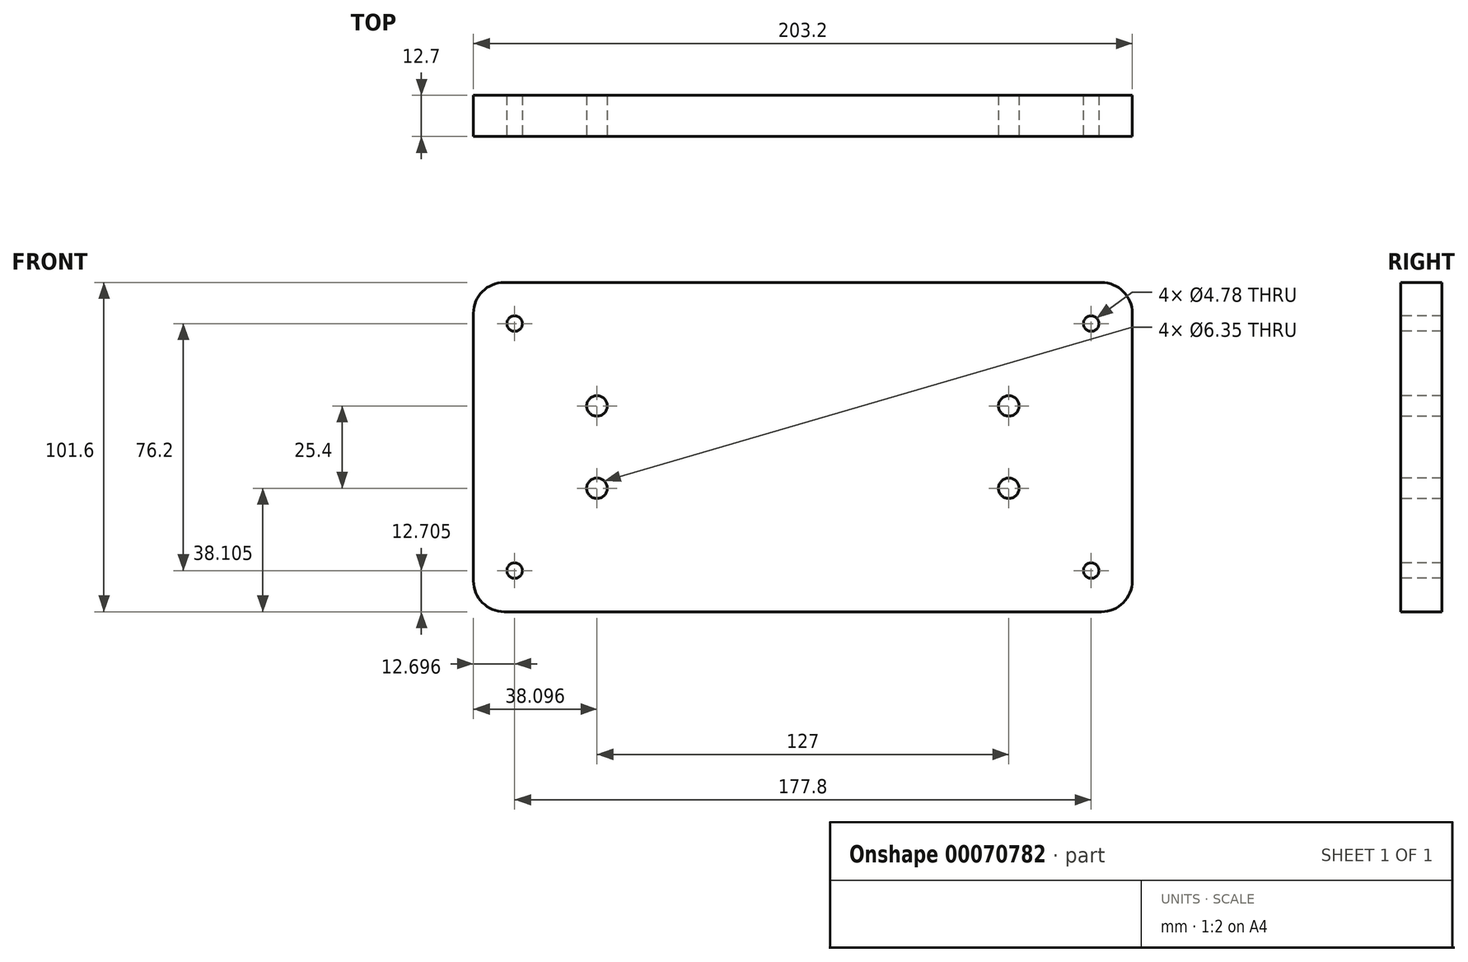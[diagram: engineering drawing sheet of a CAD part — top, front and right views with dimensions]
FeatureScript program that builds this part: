
annotation { "Feature Type Name" : "Feature", "Feature Type Description" : "" }
export const myFeature = defineFeature(function(context is Context, id is Id, definition is map)
    precondition{}
    {
        {
            var Q0;
            Q0=qCreatedBy(makeId("Front.planeOp"),FACE);
            var sketch = newSketch(context, id + "F0", { "sketchPlane" : qUnion([Q0])});
            skLineSegment(sketch, "E0.bottom", {"start": v(-101.78, -32.92) * mm, "end": v(101.42, -32.92) * mm});
            skLineSegment(sketch, "E0.top", {"start": v(-101.78, 68.68) * mm, "end": v(101.42, 68.68) * mm});
            skLineSegment(sketch, "E0.left", {"start": v(-101.78, -32.92) * mm, "end": v(-101.78, 68.68) * mm});
            skLineSegment(sketch, "E0.right", {"start": v(101.42, -32.92) * mm, "end": v(101.42, 68.68) * mm});
            skSolve(sketch);
        }
        {
            var Q0;
            Q0 = qSketchRegion(id + "F0", true);
            extrude(context, id + "F1", {"entities" : qUnion([Q0]), "depth" : 12.7 * mm});
        }
        {
            var Q0;
            Q0=makeQuery(id+"F1.opExtrude","SWEPT_EDGE",EDGE,{"disambiguationData":[OSD([sQuery(id+"F0.wireOp",EDGE,"E0.top"),sQuery(id+"F0.wireOp",EDGE,"E0.left")])]});
            var Q1;
            Q1=makeQuery(id+"F1.opExtrude","SWEPT_EDGE",EDGE,{"disambiguationData":[OSD([sQuery(id+"F0.wireOp",EDGE,"E0.top"),sQuery(id+"F0.wireOp",EDGE,"E0.right")])]});
            var Q2;
            Q2=makeQuery(id+"F1.opExtrude","SWEPT_EDGE",EDGE,{"disambiguationData":[OSD([sQuery(id+"F0.wireOp",EDGE,"E0.bottom"),sQuery(id+"F0.wireOp",EDGE,"E0.right")])]});
            var Q3;
            Q3=makeQuery(id+"F1.opExtrude","SWEPT_EDGE",EDGE,{"disambiguationData":[OSD([sQuery(id+"F0.wireOp",EDGE,"E0.bottom"),sQuery(id+"F0.wireOp",EDGE,"E0.left")])]});
            fillet(context, id + "F2", {"entities" : qUnion([Q0, Q1, Q2, Q3]), "radius" : 9.52 * mm, "tangentPropagation" : true, "allowEdgeOverflow" : false});
        }
        {
            var Q0;
            Q0=makeQuery(id+"F1.opExtrude","CAP_FACE",FACE,{"disambiguationData":[OSD([sQuery(id+"F0.wireOp",EDGE,"E0.bottom"),sQuery(id+"F0.wireOp",EDGE,"E0.top"),sQuery(id+"F0.wireOp",EDGE,"E0.left"),sQuery(id+"F0.wireOp",EDGE,"E0.right")])],"isStart":false});
            var sketch = newSketch(context, id + "F3", { "sketchPlane" : qUnion([Q0])});
            skPoint(sketch, "E1", {"position": v(-89.08, -20.22) * mm});
            skPoint(sketch, "E2", {"position": v(-89.08, 55.98) * mm});
            skPoint(sketch, "E3", {"position": v(88.72, 55.98) * mm});
            skPoint(sketch, "E4", {"position": v(88.72, -20.22) * mm});
            skSolve(sketch);
        }
        {
            var Q0;
            Q0=sQuery(id+"F3.wireOp",VERTEX,"E2");
            var Q1;
            Q1=sQuery(id+"F3.wireOp",VERTEX,"E1");
            var Q2;
            Q2=sQuery(id+"F3.wireOp",VERTEX,"E4");
            var Q3;
            Q3=sQuery(id+"F3.wireOp",VERTEX,"E3");
            var Q4;
            Q4=makeQuery(id+"F1.opExtrude","SWEPT_BODY",BODY,{"disambiguationData":[OSD([sQuery(id+"F0.wireOp",EDGE,"E0.bottom"),sQuery(id+"F0.wireOp",EDGE,"E0.top"),sQuery(id+"F0.wireOp",EDGE,"E0.left"),sQuery(id+"F0.wireOp",EDGE,"E0.right")])]});
            hole(context, id + "F4", {"style" : HoleStyle.SIMPLE, "holeDiameter" : 4.78 * mm, "endStyle" : HoleEndStyle.THROUGH, "locations" : qUnion([Q0, Q1, Q2, Q3]), "scope" : qUnion([Q4])});
        }
        {
            var Q0;
            Q0=makeQuery(id+"F1.opExtrude","CAP_FACE",FACE,{"disambiguationData":[OSD([sQuery(id+"F0.wireOp",EDGE,"E0.bottom"),sQuery(id+"F0.wireOp",EDGE,"E0.top"),sQuery(id+"F0.wireOp",EDGE,"E0.left"),sQuery(id+"F0.wireOp",EDGE,"E0.right")])],"isStart":false});
            var sketch = newSketch(context, id + "F5", { "sketchPlane" : qUnion([Q0])});
            skPoint(sketch, "E5", {"position": v(-63.68, 30.58) * mm});
            skPoint(sketch, "E6", {"position": v(-63.68, 5.18) * mm});
            skPoint(sketch, "E7", {"position": v(63.32, 30.58) * mm});
            skPoint(sketch, "E8", {"position": v(63.32, 5.18) * mm});
            skSolve(sketch);
        }
        {
            var Q0;
            Q0=sQuery(id+"F5.wireOp",VERTEX,"E5");
            var Q1;
            Q1=sQuery(id+"F5.wireOp",VERTEX,"E6");
            var Q2;
            Q2=sQuery(id+"F5.wireOp",VERTEX,"E8");
            var Q3;
            Q3=sQuery(id+"F5.wireOp",VERTEX,"E7");
            var Q4;
            Q4=makeQuery(id+"F1.opExtrude","SWEPT_BODY",BODY,{"disambiguationData":[OSD([sQuery(id+"F0.wireOp",EDGE,"E0.bottom"),sQuery(id+"F0.wireOp",EDGE,"E0.top"),sQuery(id+"F0.wireOp",EDGE,"E0.left"),sQuery(id+"F0.wireOp",EDGE,"E0.right")])]});
            hole(context, id + "F6", {"style" : HoleStyle.SIMPLE, "holeDiameter" : 6.35 * mm, "endStyle" : HoleEndStyle.THROUGH, "locations" : qUnion([Q0, Q1, Q2, Q3]), "scope" : qUnion([Q4])});
        }
    });
